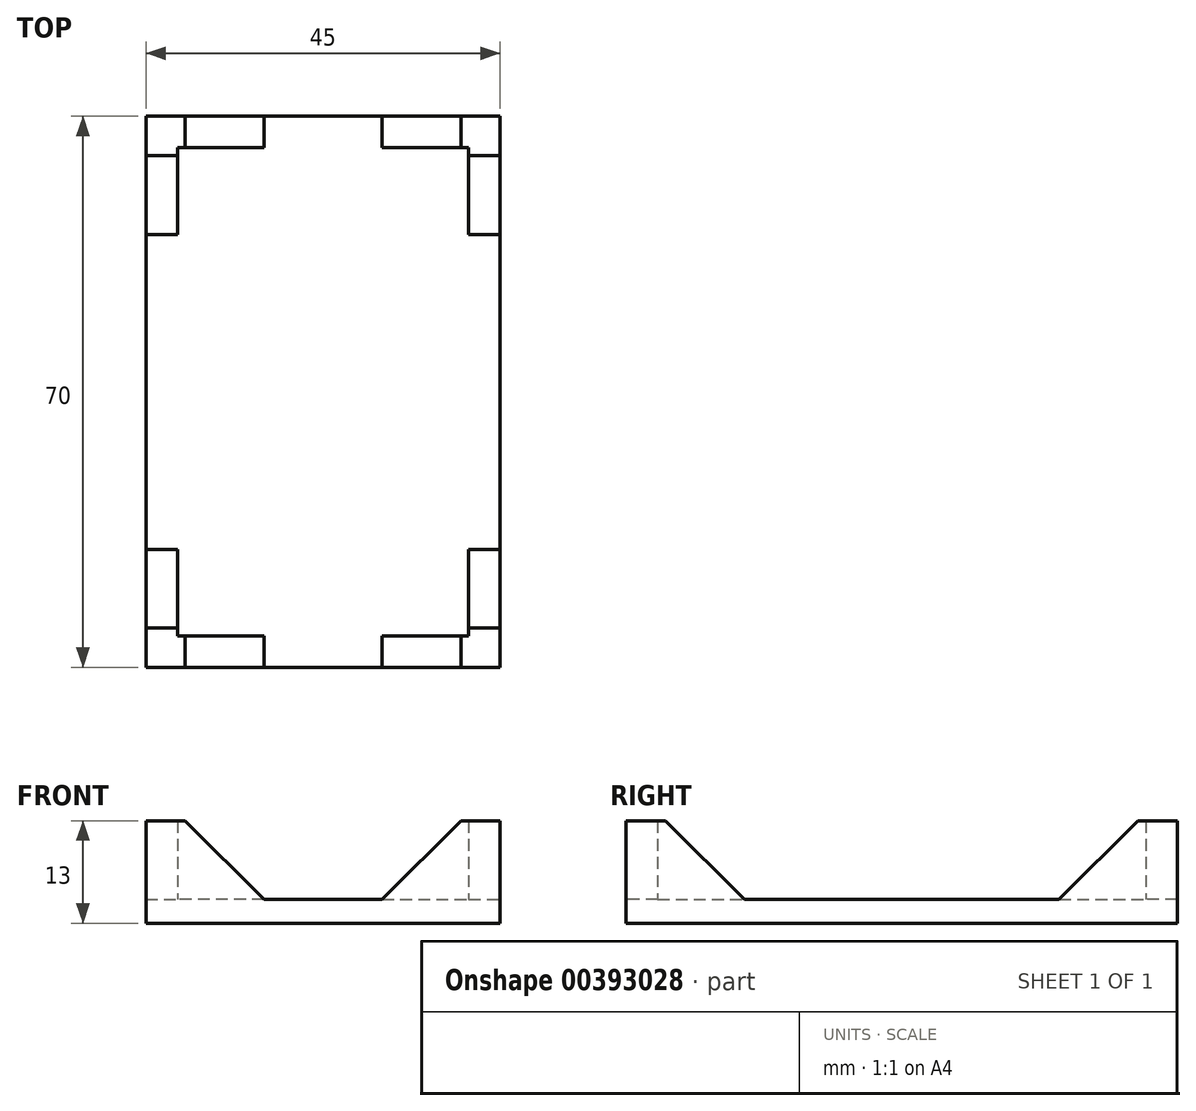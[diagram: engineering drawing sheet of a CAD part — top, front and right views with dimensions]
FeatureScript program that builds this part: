
annotation { "Feature Type Name" : "Feature", "Feature Type Description" : "" }
export const myFeature = defineFeature(function(context is Context, id is Id, definition is map)
    precondition{}
    {
        {
            var Q0;
            Q0=qCreatedBy(makeId("Top.planeOp"),FACE);
            var sketch = newSketch(context, id + "F0", { "sketchPlane" : qUnion([Q0])});
            skLineSegment(sketch, "E0.bottom", {"start": v(-22.5, 35) * mm, "end": v(22.5, 35) * mm});
            skLineSegment(sketch, "E0.top", {"start": v(-22.5, -35) * mm, "end": v(22.5, -35) * mm});
            skLineSegment(sketch, "E0.left", {"start": v(-22.5, 35) * mm, "end": v(-22.5, -35) * mm});
            skLineSegment(sketch, "E0.right", {"start": v(22.5, 35) * mm, "end": v(22.5, -35) * mm});
            skPoint(sketch, "E0.middle", {"position": v(0, 0) * mm});
            skSolve(sketch);
        }
        {
            var Q0;
            Q0=makeQuery(id+"F0.imprint","IMPRINT",FACE,{"disambiguationData":[TD([[makeQuery(id+"F0.imprint","IMPRINT",EDGE,{"derivedFrom":sQuery(id+"F0.wireOp",EDGE,"E0.bottom")}),-1.0]])]});
            extrude(context, id + "F1", {"entities" : qUnion([Q0]), "depth" : 3 * mm});
        }
        {
            var Q0;
            Q0=makeQuery(id+"F1.opExtrude","CAP_FACE",FACE,{"disambiguationData":[OSD([sQuery(id+"F0.wireOp",EDGE,"E0.bottom"),sQuery(id+"F0.wireOp",EDGE,"E0.top"),sQuery(id+"F0.wireOp",EDGE,"E0.left"),sQuery(id+"F0.wireOp",EDGE,"E0.right")])],"isStart":false});
            var sketch = newSketch(context, id + "F2", { "sketchPlane" : qUnion([Q0])});
            skLineSegment(sketch, "E1.0", {"start": v(-18.5, 31) * mm, "end": v(-18.5, -31) * mm});
            skLineSegment(sketch, "E1.1", {"start": v(18.5, 31) * mm, "end": v(-18.5, 31) * mm});
            skLineSegment(sketch, "E1.2", {"start": v(18.5, -31) * mm, "end": v(18.5, 31) * mm});
            skLineSegment(sketch, "E1.3", {"start": v(-18.5, -31) * mm, "end": v(18.5, -31) * mm});
            skLineSegment(sketch, "E2", {"start": v(-22.5, 35) * mm, "end": v(-7.5, 35) * mm, "construction": true});
            skLineSegment(sketch, "E3", {"start": v(-22.5, 35) * mm, "end": v(-22.5, 20) * mm, "construction": true});
            skLineSegment(sketch, "E4", {"start": v(22.5, 35) * mm, "end": v(7.5, 35) * mm, "construction": true});
            skLineSegment(sketch, "E5", {"start": v(-22.5, -35) * mm, "end": v(-22.5, -20) * mm, "construction": true});
            skLineSegment(sketch, "E6", {"start": v(-22.5, 20) * mm, "end": v(22.5, 20) * mm});
            skLineSegment(sketch, "E7", {"start": v(-7.5, 35) * mm, "end": v(-7.5, -35) * mm});
            skLineSegment(sketch, "E8", {"start": v(7.5, 35) * mm, "end": v(7.5, -35) * mm});
            skLineSegment(sketch, "E9", {"start": v(-22.5, -20) * mm, "end": v(22.5, -20) * mm});
            skSolve(sketch);
        }
        {
            var Q0;
            {var subQ3=sQuery(id+"F2.wireOp",EDGE,"E1.1");var subQ8=sQuery(id+"F2.wireOp",EDGE,"E1.0");var subQ10=makeQuery(id+"F2.imprint","INTERSECT",VERTEX,{"derivedFrom":[subQ8,subQ3]});Q0=makeQuery(id+"F2.imprint","IMPRINT",FACE,{"disambiguationData":[TD([[makeQuery(id+"F2.imprint","IMPRINT",EDGE,{"disambiguationData":[TD([[subQ10,-1.0]])],"derivedFrom":subQ8}),-1.0]])]});}
            var Q1;
            {var subQ3=sQuery(id+"F2.wireOp",EDGE,"E1.1");var subQ9=sQuery(id+"F2.wireOp",EDGE,"E1.2");var subQ11=makeQuery(id+"F2.imprint","INTERSECT",VERTEX,{"derivedFrom":[subQ3,subQ9]});Q1=makeQuery(id+"F2.imprint","IMPRINT",FACE,{"disambiguationData":[TD([[makeQuery(id+"F2.imprint","IMPRINT",EDGE,{"disambiguationData":[TD([[subQ11,-1.0]])],"derivedFrom":subQ3}),-1.0]])]});}
            var Q2;
            {var subQ3=sQuery(id+"F2.wireOp",EDGE,"E1.2");var subQ9=sQuery(id+"F2.wireOp",EDGE,"E1.3");var subQ11=makeQuery(id+"F2.imprint","INTERSECT",VERTEX,{"derivedFrom":[subQ3,subQ9]});Q2=makeQuery(id+"F2.imprint","IMPRINT",FACE,{"disambiguationData":[TD([[makeQuery(id+"F2.imprint","IMPRINT",EDGE,{"disambiguationData":[TD([[subQ11,-1.0]])],"derivedFrom":subQ3}),-1.0]])]});}
            var Q3;
            {var subQ3=sQuery(id+"F2.wireOp",EDGE,"E1.3");var subQ5=sQuery(id+"F2.wireOp",EDGE,"E1.0");var subQ6=makeQuery(id+"F2.imprint","INTERSECT",VERTEX,{"derivedFrom":[subQ5,subQ3]});Q3=makeQuery(id+"F2.imprint","IMPRINT",FACE,{"disambiguationData":[TD([[makeQuery(id+"F2.imprint","IMPRINT",EDGE,{"disambiguationData":[TD([[subQ6,1.0]])],"derivedFrom":subQ5}),-1.0]])]});}
            extrude(context, id + "F3", {"entities" : qUnion([Q0, Q1, Q2, Q3]), "operationType" : NewBodyOperationType.ADD, "depth" : 10 * mm});
        }
        {
            var Q0;
            {var subQ0=sQuery(id+"F2.wireOp",EDGE,"E7");Q0=makeQuery(id+"F3.opExtrude","CAP_EDGE",EDGE,{"disambiguationData":[OSD([subQ0]),TDD([makeQuery(id+"F2.imprint","IMPRINT",EDGE,{"disambiguationData":[TD([[makeQuery(id+"F2.imprint","INTERSECT",VERTEX,{"derivedFrom":[makeQuery(id+"F1.opExtrude","CAP_EDGE",EDGE,{"disambiguationData":[OSD([sQuery(id+"F0.wireOp",EDGE,"E0.bottom")])],"isStart":false}),subQ0]}),-1.0]])],"derivedFrom":subQ0})])],"isStart":false});}
            var Q1;
            {var subQ0=sQuery(id+"F2.wireOp",EDGE,"E7");Q1=makeQuery(id+"F3.opExtrude","CAP_EDGE",EDGE,{"disambiguationData":[OSD([subQ0]),TDD([makeQuery(id+"F2.imprint","IMPRINT",EDGE,{"disambiguationData":[TD([[makeQuery(id+"F2.imprint","INTERSECT",VERTEX,{"derivedFrom":[makeQuery(id+"F1.opExtrude","CAP_EDGE",EDGE,{"disambiguationData":[OSD([sQuery(id+"F0.wireOp",EDGE,"E0.top")])],"isStart":false}),subQ0]}),1.0]])],"derivedFrom":subQ0})])],"isStart":false});}
            var Q2;
            {var subQ0=sQuery(id+"F2.wireOp",EDGE,"E9");Q2=makeQuery(id+"F3.opExtrude","CAP_EDGE",EDGE,{"disambiguationData":[OSD([subQ0]),TDD([makeQuery(id+"F2.imprint","IMPRINT",EDGE,{"disambiguationData":[TD([[makeQuery(id+"F2.imprint","INTERSECT",VERTEX,{"derivedFrom":[makeQuery(id+"F1.opExtrude","CAP_EDGE",EDGE,{"disambiguationData":[OSD([sQuery(id+"F0.wireOp",EDGE,"E0.left")])],"isStart":false}),subQ0]}),-1.0]])],"derivedFrom":subQ0})])],"isStart":false});}
            var Q3;
            {var subQ0=sQuery(id+"F2.wireOp",EDGE,"E9");Q3=makeQuery(id+"F3.opExtrude","CAP_EDGE",EDGE,{"disambiguationData":[OSD([subQ0]),TDD([makeQuery(id+"F2.imprint","IMPRINT",EDGE,{"disambiguationData":[TD([[makeQuery(id+"F2.imprint","INTERSECT",VERTEX,{"derivedFrom":[makeQuery(id+"F1.opExtrude","CAP_EDGE",EDGE,{"disambiguationData":[OSD([sQuery(id+"F0.wireOp",EDGE,"E0.right")])],"isStart":false}),subQ0]}),1.0]])],"derivedFrom":subQ0})])],"isStart":false});}
            var Q4;
            {var subQ0=sQuery(id+"F2.wireOp",EDGE,"E6");Q4=makeQuery(id+"F3.opExtrude","CAP_EDGE",EDGE,{"disambiguationData":[OSD([subQ0]),TDD([makeQuery(id+"F2.imprint","IMPRINT",EDGE,{"disambiguationData":[TD([[makeQuery(id+"F2.imprint","INTERSECT",VERTEX,{"derivedFrom":[makeQuery(id+"F1.opExtrude","CAP_EDGE",EDGE,{"disambiguationData":[OSD([sQuery(id+"F0.wireOp",EDGE,"E0.right")])],"isStart":false}),subQ0]}),1.0]])],"derivedFrom":subQ0})])],"isStart":false});}
            var Q5;
            {var subQ0=sQuery(id+"F2.wireOp",EDGE,"E6");Q5=makeQuery(id+"F3.opExtrude","CAP_EDGE",EDGE,{"disambiguationData":[OSD([subQ0]),TDD([makeQuery(id+"F2.imprint","IMPRINT",EDGE,{"disambiguationData":[TD([[makeQuery(id+"F2.imprint","INTERSECT",VERTEX,{"derivedFrom":[makeQuery(id+"F1.opExtrude","CAP_EDGE",EDGE,{"disambiguationData":[OSD([sQuery(id+"F0.wireOp",EDGE,"E0.left")])],"isStart":false}),subQ0]}),-1.0]])],"derivedFrom":subQ0})])],"isStart":false});}
            var Q6;
            {var subQ0=sQuery(id+"F2.wireOp",EDGE,"E8");Q6=makeQuery(id+"F3.opExtrude","CAP_EDGE",EDGE,{"disambiguationData":[OSD([subQ0]),TDD([makeQuery(id+"F2.imprint","IMPRINT",EDGE,{"disambiguationData":[TD([[makeQuery(id+"F2.imprint","INTERSECT",VERTEX,{"derivedFrom":[makeQuery(id+"F1.opExtrude","CAP_EDGE",EDGE,{"disambiguationData":[OSD([sQuery(id+"F0.wireOp",EDGE,"E0.top")])],"isStart":false}),subQ0]}),1.0]])],"derivedFrom":subQ0})])],"isStart":false});}
            var Q7;
            {var subQ0=sQuery(id+"F2.wireOp",EDGE,"E8");Q7=makeQuery(id+"F3.opExtrude","CAP_EDGE",EDGE,{"disambiguationData":[OSD([subQ0]),TDD([makeQuery(id+"F2.imprint","IMPRINT",EDGE,{"disambiguationData":[TD([[makeQuery(id+"F2.imprint","INTERSECT",VERTEX,{"derivedFrom":[makeQuery(id+"F1.opExtrude","CAP_EDGE",EDGE,{"disambiguationData":[OSD([sQuery(id+"F0.wireOp",EDGE,"E0.bottom")])],"isStart":false}),subQ0]}),-1.0]])],"derivedFrom":subQ0})])],"isStart":false});}
            chamfer(context, id + "F4", {"entities" : qUnion([Q0, Q1, Q2, Q3, Q4, Q5, Q6, Q7]), "width" : 10 * mm, "tangentPropagation" : true});
        }
    });
